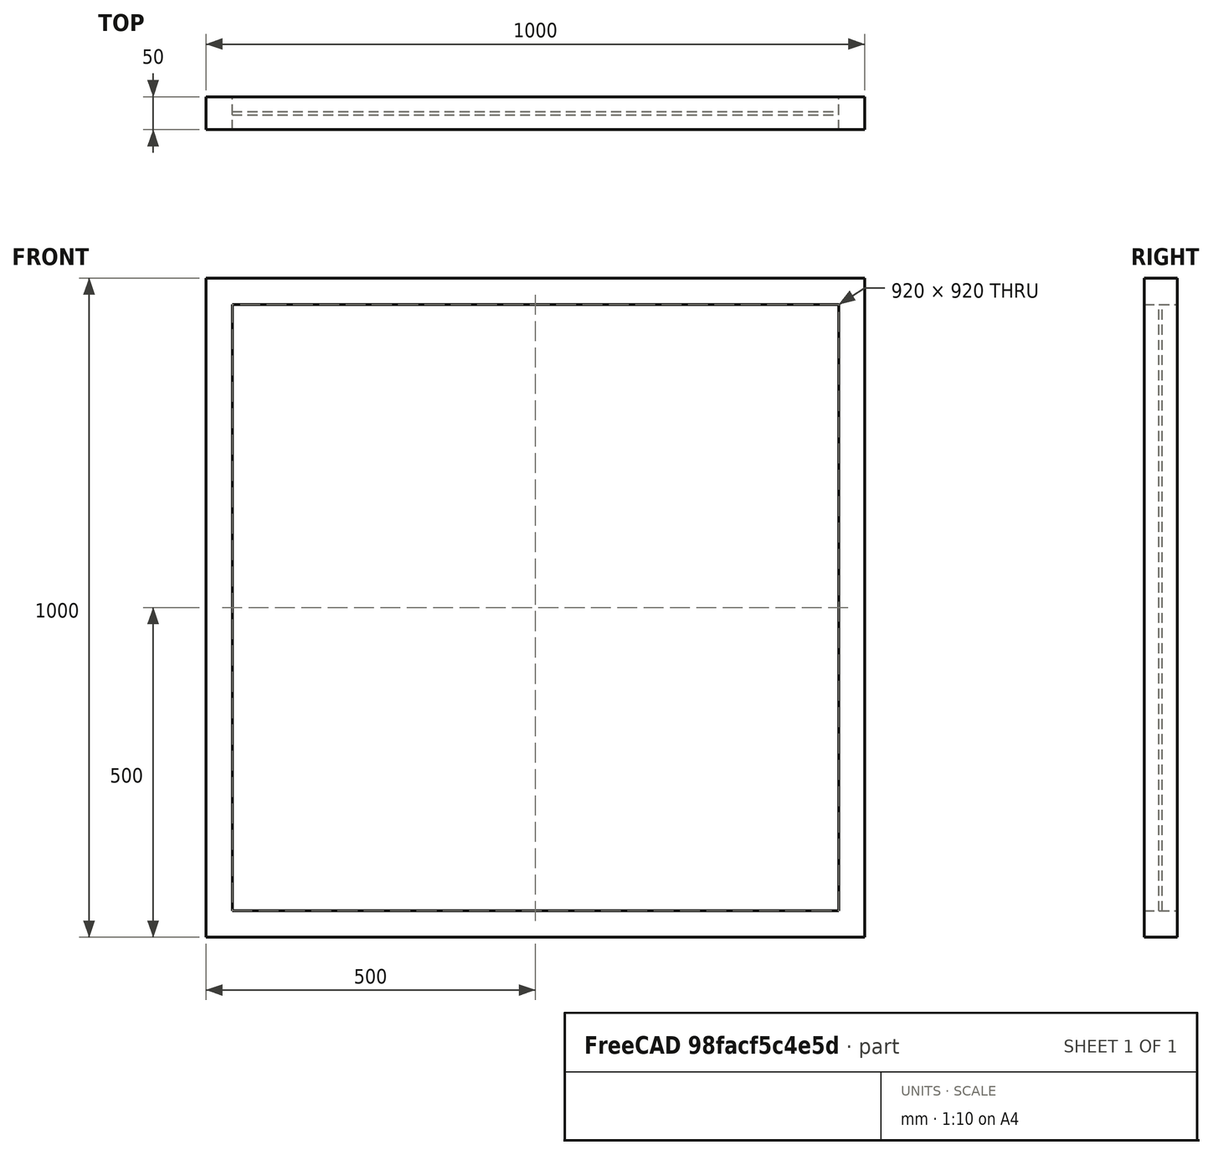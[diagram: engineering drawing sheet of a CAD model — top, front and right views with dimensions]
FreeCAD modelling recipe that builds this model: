
FCSTD DOCUMENT  (FreeCAD 0.16R6704 (Git))
Label: Simple window fixed
License: CreativeCommons Attribution
LicenseURL: http://creativecommons.org/licenses/by/4.0/
objects: Sketcher::SketchObject×1, Part::FeaturePython×1
note: 2 computed .brp shape members not serialized (recipe doc carries the construction recipe); baked Part::Feature solids carry a one-line shape summary decoded from their .brp

FEATURE [Sketcher::SketchObject] Sketch091
  Placement = pos=(0,0,0) rot=(1,0,0;1.5708rad)
  sketch-geometry (12):
    g0: LineSegment StartX=0 StartY=0 StartZ=0 EndX=1000 EndY=0 EndZ=0
    g1: LineSegment StartX=1000 StartY=0 StartZ=0 EndX=1000 EndY=1000 EndZ=0
    g2: LineSegment StartX=1000 StartY=1000 StartZ=0 EndX=0 EndY=1000 EndZ=0
    g3: LineSegment StartX=0 StartY=1000 StartZ=0 EndX=0 EndY=0 EndZ=0
    g4: LineSegment StartX=40 StartY=40 StartZ=0 EndX=960 EndY=40 EndZ=0
    g5: LineSegment StartX=960 StartY=40 StartZ=0 EndX=960 EndY=960 EndZ=0
    g6: LineSegment StartX=960 StartY=960 StartZ=0 EndX=40 EndY=960 EndZ=0
    g7: LineSegment StartX=40 StartY=960 StartZ=0 EndX=40 EndY=40 EndZ=0
    g8: LineSegment [constr] StartX=0 StartY=970.406 StartZ=0 EndX=40 EndY=970.406 EndZ=0
    g9: LineSegment [constr] StartX=960 StartY=933.123 StartZ=0 EndX=1000 EndY=933.123 EndZ=0
    g10: LineSegment [constr] StartX=649.298 StartY=1000 StartZ=0 EndX=649.298 EndY=960 EndZ=0
    g11: LineSegment [constr] StartX=547.783 StartY=40 StartZ=0 EndX=547.783 EndY=0 EndZ=0
  constraints (35):
    c: Coincident(g0,g1)
    c: Coincident(g1,g2)
    c: Coincident(g2,g3)
    c: Coincident(g3,g0)
    c: Horizontal(g0)
    c: Horizontal(g2)
    c: Vertical(g1)
    c: Vertical(g3)
    c: Coincident(g4,g5)
    c: Coincident(g5,g6)
    c: Coincident(g6,g7)
    c: Coincident(g7,g4)
    c: Horizontal(g4)
    c: Horizontal(g6)
    c: Vertical(g5)
    c: Vertical(g7)
    c: DistanceY(g1) = 1000  'Altura vão'
    c: DistanceX(g0) = 1000  'Largura vão'
    c: DistanceX(g2,g6) = 40  'Largura pefis'
    c: Coincident(g0,g-1)  'Constraint20'
    c: PointOnObject(g8,g3)
    c: PointOnObject(g8,g7)
    c: PointOnObject(g9,g5)
    c: PointOnObject(g9,g1)
    c: PointOnObject(g10,g2)
    c: PointOnObject(g10,g6)
    c: PointOnObject(g11,g4)
    c: PointOnObject(g11,g0)
    c: Equal(g8,g10)
    c: Equal(g10,g9)
    c: Equal(g9,g11)
    c: Angle(g8) = 0
    c: Angle(g10) = -1.5708
    c: Angle(g9) = 0
    c: Angle(g11) = -1.5708
FEATURE [Part::FeaturePython] Window071  label="Simple window fixed"  # WARN: FeaturePython — macro-defined, semantics opaque (R4)
  Base = -> Sketch091
  Height = 1000
  HoleDepth = 0
  MoveWithHost = true
  Normal = (0,1,0)
  Preset = 1
  Role = 0
  Width = 1000
  WindowParts = MONTANTES | Frame | Wire0,Wire1 | 50.0 | 0.0 | VIDRO | Glass panel | Wire1 | 5.0 | 22.5
